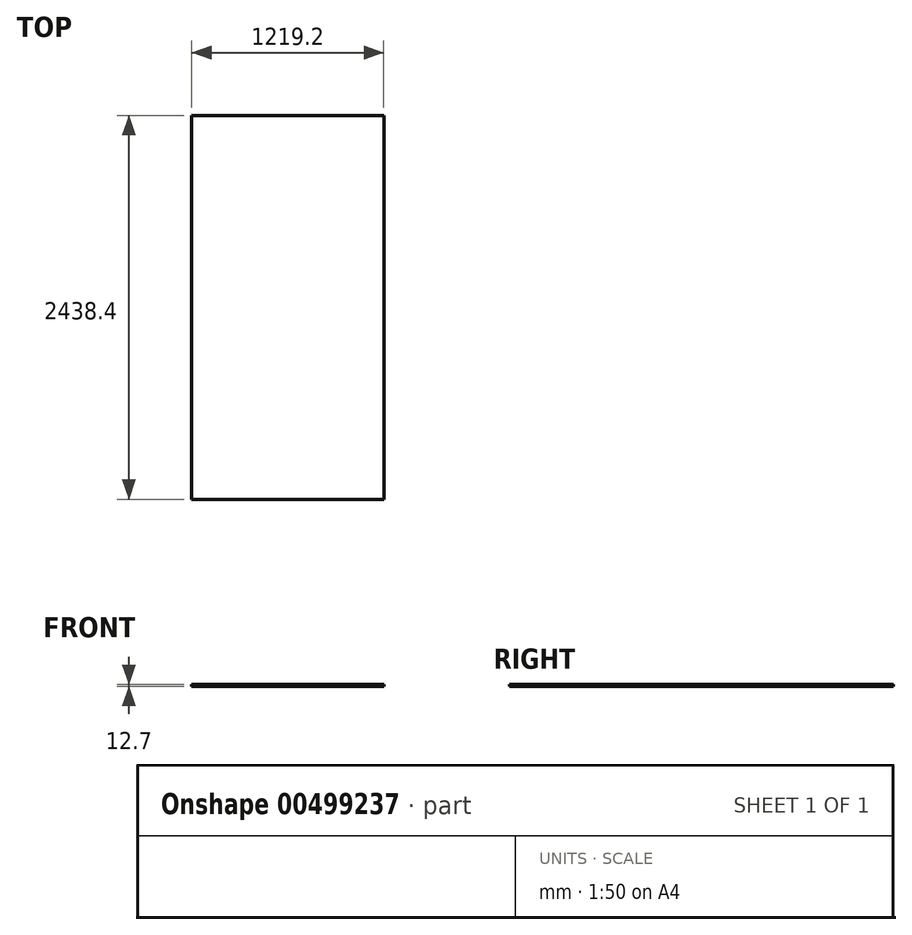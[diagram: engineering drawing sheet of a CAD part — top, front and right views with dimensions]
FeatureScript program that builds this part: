
annotation { "Feature Type Name" : "Feature", "Feature Type Description" : "" }
export const myFeature = defineFeature(function(context is Context, id is Id, definition is map)
    precondition{}
    {
        {
            var Q0;
            Q0=qCreatedBy(makeId("Top.planeOp"),FACE);
            var sketch = newSketch(context, id + "F0", { "sketchPlane" : qUnion([Q0])});
            skLineSegment(sketch, "E0.bottom", {"start": v(-607.09, 1899.67) * mm, "end": v(612.11, 1899.67) * mm});
            skLineSegment(sketch, "E0.top", {"start": v(-607.09, -538.73) * mm, "end": v(612.11, -538.73) * mm});
            skLineSegment(sketch, "E0.left", {"start": v(-607.09, 1899.67) * mm, "end": v(-607.09, -538.73) * mm});
            skLineSegment(sketch, "E0.right", {"start": v(612.11, 1899.67) * mm, "end": v(612.11, -538.73) * mm});
            skSolve(sketch);
        }
        {
            var Q0;
            Q0 = qSketchRegion(id + "F0", true);
            extrude(context, id + "F1", {"entities" : qUnion([Q0]), "depth" : 12.7 * mm, "offsetDistance" : 25.4 * mm});
        }
    });
